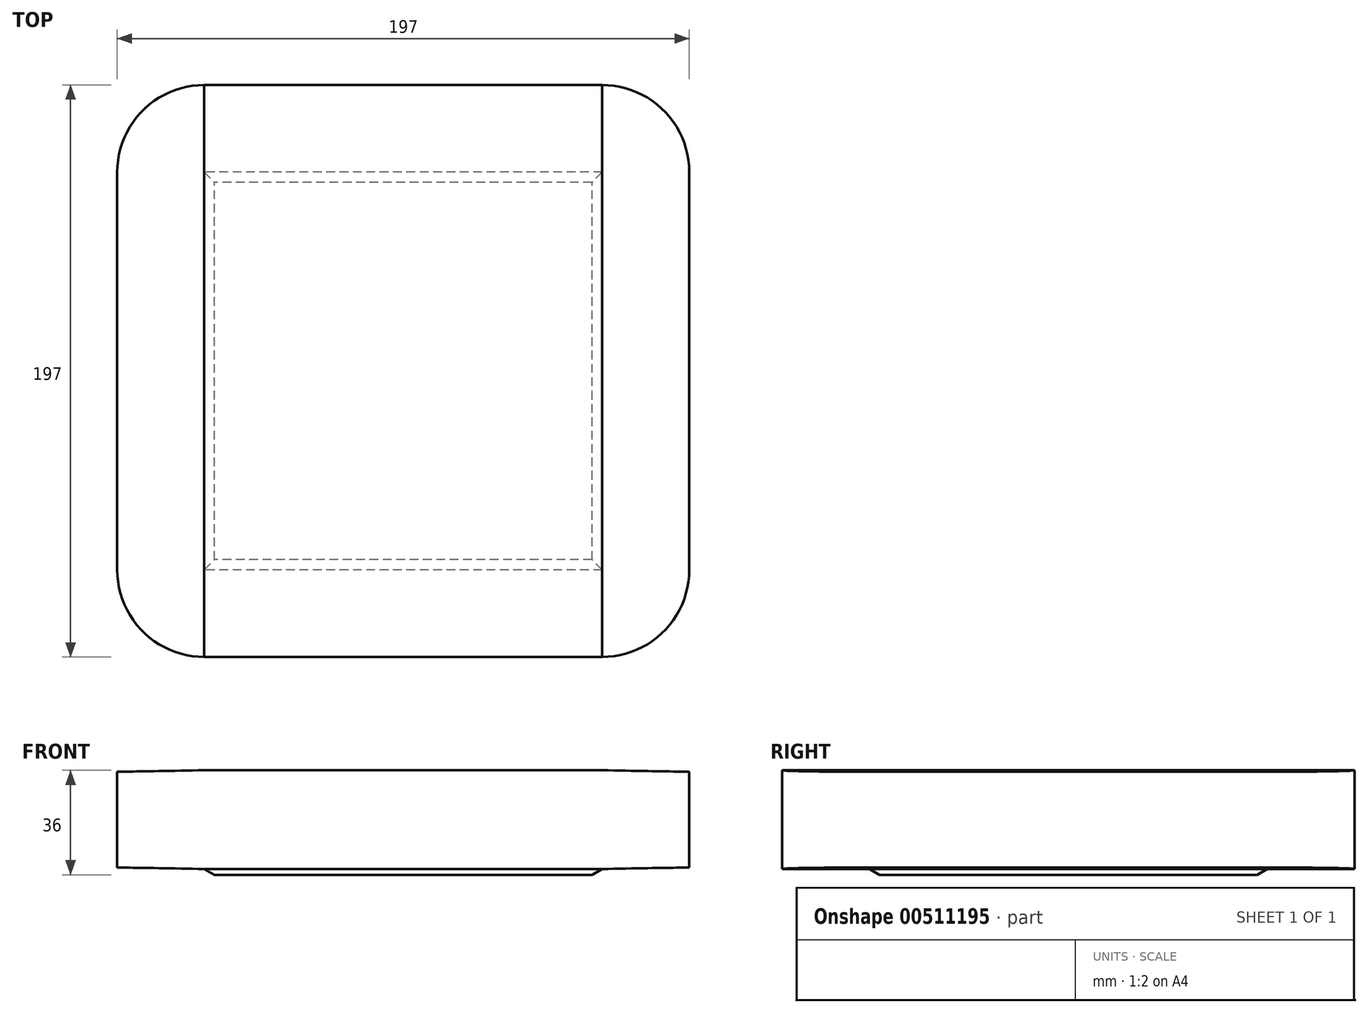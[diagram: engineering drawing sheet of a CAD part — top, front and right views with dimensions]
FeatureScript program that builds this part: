
annotation { "Feature Type Name" : "Feature", "Feature Type Description" : "" }
export const myFeature = defineFeature(function(context is Context, id is Id, definition is map)
    precondition{}
    {
        {
            var Q0;
            Q0=qCreatedBy(makeId("Top.planeOp"),FACE);
            var sketch = newSketch(context, id + "F0", { "sketchPlane" : qUnion([Q0])});
            skLineSegment(sketch, "E0.bottom", {"start": v(0, 0) * mm, "end": v(197, 0) * mm});
            skLineSegment(sketch, "E0.top", {"start": v(0, -197) * mm, "end": v(197, -197) * mm});
            skLineSegment(sketch, "E0.left", {"start": v(0, 0) * mm, "end": v(0, -197) * mm});
            skLineSegment(sketch, "E0.right", {"start": v(197, 0) * mm, "end": v(197, -197) * mm});
            skSolve(sketch);
        }
        {
            var Q0;
            Q0 = qSketchRegion(id + "F0", true);
            extrude(context, id + "F1", {"entities" : qUnion([Q0]), "depth" : 34 * mm});
        }
        {
            var Q0;
            Q0=makeQuery(id+"F1.opExtrude","SWEPT_EDGE",EDGE,{"disambiguationData":[OSD([sQuery(id+"F0.wireOp",EDGE,"E0.top"),sQuery(id+"F0.wireOp",EDGE,"E0.right")])]});
            var Q1;
            Q1=makeQuery(id+"F1.opExtrude","SWEPT_EDGE",EDGE,{"disambiguationData":[OSD([sQuery(id+"F0.wireOp",EDGE,"E0.bottom"),sQuery(id+"F0.wireOp",EDGE,"E0.right")])]});
            var Q2;
            Q2=makeQuery(id+"F1.opExtrude","SWEPT_EDGE",EDGE,{"disambiguationData":[OSD([sQuery(id+"F0.wireOp",EDGE,"E0.bottom"),sQuery(id+"F0.wireOp",EDGE,"E0.left")])]});
            var Q3;
            Q3=makeQuery(id+"F1.opExtrude","SWEPT_EDGE",EDGE,{"disambiguationData":[OSD([sQuery(id+"F0.wireOp",EDGE,"E0.top"),sQuery(id+"F0.wireOp",EDGE,"E0.left")])]});
            fillet(context, id + "F2", {"entities" : qUnion([Q0, Q1, Q2, Q3]), "radius" : 30 * mm, "tangentPropagation" : true, "allowEdgeOverflow" : false});
        }
        {
            var Q0;
            Q0=qCreatedBy(makeId("Front.planeOp"),FACE);
            cPlane(context, id + "F3", {"entities" : qUnion([Q0]), "cplaneType" : CPlaneType.OFFSET, "offset" : 197 * mm, "width" : 150 * mm, "height" : 150 * mm});
        }
        {
            var Q0;
            Q0=qCreatedBy(id+"F3.planeOp",FACE);
            var sketch = newSketch(context, id + "F4", { "sketchPlane" : qUnion([Q0])});
            skLineSegment(sketch, "E1", {"start": v(167, 34) * mm, "end": v(197, 34) * mm});
            skLineSegment(sketch, "E2", {"start": v(167, 34) * mm, "end": v(197, 33.48) * mm});
            skLineSegment(sketch, "E3", {"start": v(197, 34) * mm, "end": v(197, 33.48) * mm});
            skLineSegment(sketch, "E4", {"start": v(0, 0) * mm, "end": v(197, 0) * mm});
            skLineSegment(sketch, "E5", {"start": v(98.5, 0) * mm, "end": v(98.5, 31) * mm});
            skLineSegment(sketch, "E6", {"start": v(98.5, 15.5) * mm, "end": v(74.04, 15.5) * mm});
            skLineSegment(sketch, "E7.MirrorCS", {"start": v(197, 0) * mm, "end": v(197, 0.52) * mm});
            skLineSegment(sketch, "E8.MirrorCS", {"start": v(167, 0) * mm, "end": v(197, 0) * mm});
            skLineSegment(sketch, "E9.MirrorCS", {"start": v(167, 0) * mm, "end": v(197, 0.52) * mm});
            skLineSegment(sketch, "E10", {"start": v(197, 0) * mm, "end": v(167, 0) * mm});
            skLineSegment(sketch, "E11.MirrorCS", {"start": v(0, 0) * mm, "end": v(0, 0.52) * mm});
            skLineSegment(sketch, "E12.MirrorCS", {"start": v(0, 34) * mm, "end": v(0, 33.48) * mm});
            skLineSegment(sketch, "E13.MirrorCS", {"start": v(30, 34) * mm, "end": v(0, 34) * mm});
            skLineSegment(sketch, "E14.MirrorCS", {"start": v(30, 0) * mm, "end": v(0, 0) * mm});
            skLineSegment(sketch, "E15.MirrorCS", {"start": v(0, 0) * mm, "end": v(30, 0) * mm});
            skLineSegment(sketch, "E16.MirrorCS", {"start": v(30, 0) * mm, "end": v(0, 0.52) * mm});
            skLineSegment(sketch, "E17.MirrorCS", {"start": v(30, 3) * mm, "end": v(30, 34) * mm});
            skLineSegment(sketch, "E18.MirrorCS", {"start": v(30, 34) * mm, "end": v(0, 33.48) * mm});
            skSolve(sketch);
        }
        {
            var Q0;
            Q0 = qSketchRegion(id + "F4", true);
            extrude(context, id + "F5", {"entities" : qUnion([Q0]), "operationType" : NewBodyOperationType.REMOVE, "oppositeDirection" : true, "depth" : 197 * mm});
        }
        {
            var Q0;
            Q0=qCreatedBy(makeId("Top.planeOp"),FACE);
            var sketch = newSketch(context, id + "F6", { "sketchPlane" : qUnion([Q0])});
            skLineSegment(sketch, "E19", {"start": v(0, 0) * mm, "end": v(98.5, 0) * mm});
            skLineSegment(sketch, "E20", {"start": v(98.5, 0) * mm, "end": v(98.5, -98.5) * mm});
            skLineSegment(sketch, "E21.bottom", {"start": v(167, -167) * mm, "end": v(30, -167) * mm});
            skLineSegment(sketch, "E21.top", {"start": v(167, -30) * mm, "end": v(30, -30) * mm});
            skLineSegment(sketch, "E21.left", {"start": v(167, -167) * mm, "end": v(167, -30) * mm});
            skLineSegment(sketch, "E21.right", {"start": v(30, -167) * mm, "end": v(30, -30) * mm});
            skPoint(sketch, "E21.middle", {"position": v(98.5, -98.5) * mm});
            skSolve(sketch);
        }
        {
            var Q0;
            Q0=qCreatedBy(makeId("Top.planeOp"),FACE);
            cPlane(context, id + "F7", {"entities" : qUnion([Q0]), "cplaneType" : CPlaneType.OFFSET, "offset" : 2 * mm, "oppositeDirection" : true, "width" : 150 * mm, "height" : 150 * mm});
        }
        {
            var Q0;
            Q0=qCreatedBy(id+"F7.planeOp",FACE);
            var sketch = newSketch(context, id + "F8", { "sketchPlane" : qUnion([Q0])});
            skLineSegment(sketch, "E22", {"start": v(0, 0) * mm, "end": v(98.5, 0) * mm});
            skLineSegment(sketch, "E23", {"start": v(98.5, 0) * mm, "end": v(98.5, -98.5) * mm});
            skLineSegment(sketch, "E24.bottom", {"start": v(163.5, -163.5) * mm, "end": v(33.5, -163.5) * mm});
            skLineSegment(sketch, "E24.top", {"start": v(163.5, -33.5) * mm, "end": v(33.5, -33.5) * mm});
            skLineSegment(sketch, "E24.left", {"start": v(163.5, -163.5) * mm, "end": v(163.5, -33.5) * mm});
            skLineSegment(sketch, "E24.right", {"start": v(33.5, -163.5) * mm, "end": v(33.5, -33.5) * mm});
            skPoint(sketch, "E24.middle", {"position": v(98.5, -98.5) * mm});
            skSolve(sketch);
        }
        {
            var Q1;
            Q1=makeQuery(id+"F6.imprint","IMPRINT",FACE,{"disambiguationData":[TD([[makeQuery(id+"F6.imprint","IMPRINT",EDGE,{"derivedFrom":sQuery(id+"F6.wireOp",EDGE,"E21.bottom")}),-1.0]])]});
            var Q2;
            Q2=makeQuery(id+"F8.imprint","IMPRINT",FACE,{"disambiguationData":[TD([[makeQuery(id+"F8.imprint","IMPRINT",EDGE,{"derivedFrom":sQuery(id+"F8.wireOp",EDGE,"E24.bottom")}),-1.0]])]});
            loft(context, id + "F9", {"sheetProfilesArray" : [{ "sheetProfileEntities" : qUnion([Q1]) }, { "sheetProfileEntities" : qUnion([Q2]) }]});
        }
    });
